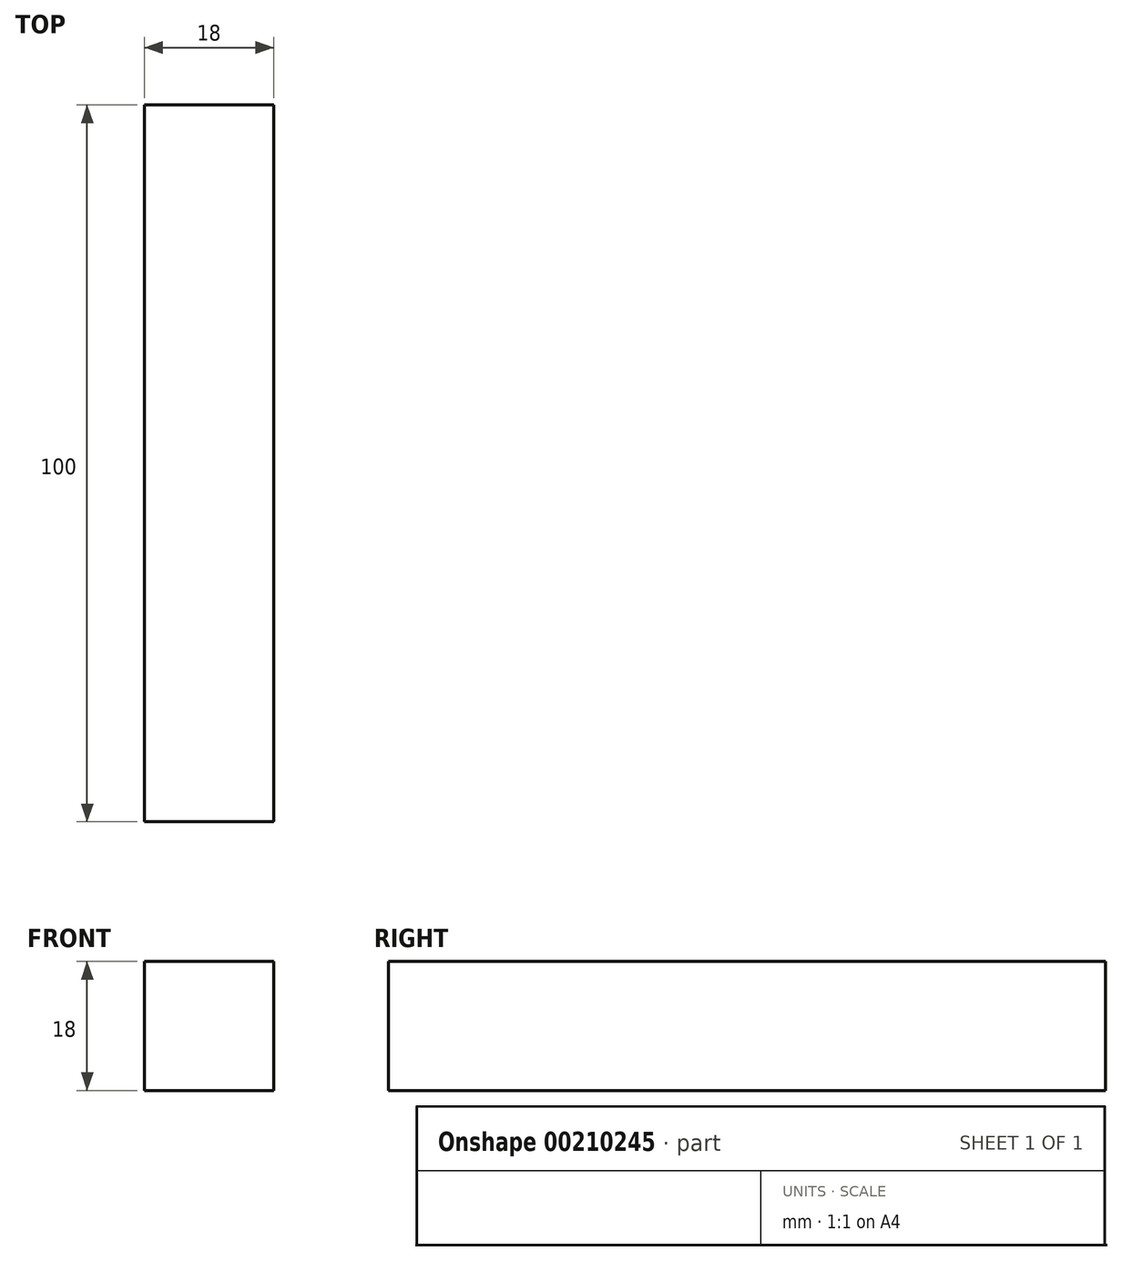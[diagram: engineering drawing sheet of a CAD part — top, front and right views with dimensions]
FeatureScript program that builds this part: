
annotation { "Feature Type Name" : "Feature", "Feature Type Description" : "" }
export const myFeature = defineFeature(function(context is Context, id is Id, definition is map)
    precondition{}
    {
        {
            var Q0;
            Q0=qCreatedBy(makeId("Front.planeOp"),FACE);
            var sketch = newSketch(context, id + "F0", { "sketchPlane" : qUnion([Q0])});
            skLineSegment(sketch, "E0.bottom", {"start": v(9, 9) * mm, "end": v(-9, 9) * mm});
            skLineSegment(sketch, "E0.top", {"start": v(9, -9) * mm, "end": v(-9, -9) * mm});
            skLineSegment(sketch, "E0.left", {"start": v(9, 9) * mm, "end": v(9, -9) * mm});
            skLineSegment(sketch, "E0.right", {"start": v(-9, 9) * mm, "end": v(-9, -9) * mm});
            skPoint(sketch, "E0.middle", {"position": v(0, 0) * mm});
            skSolve(sketch);
        }
        {
            var Q0;
            Q0 = qSketchRegion(id + "F0", true);
            extrude(context, id + "F1", {"entities" : qUnion([Q0]), "depth" : 100 * mm});
        }
    });
